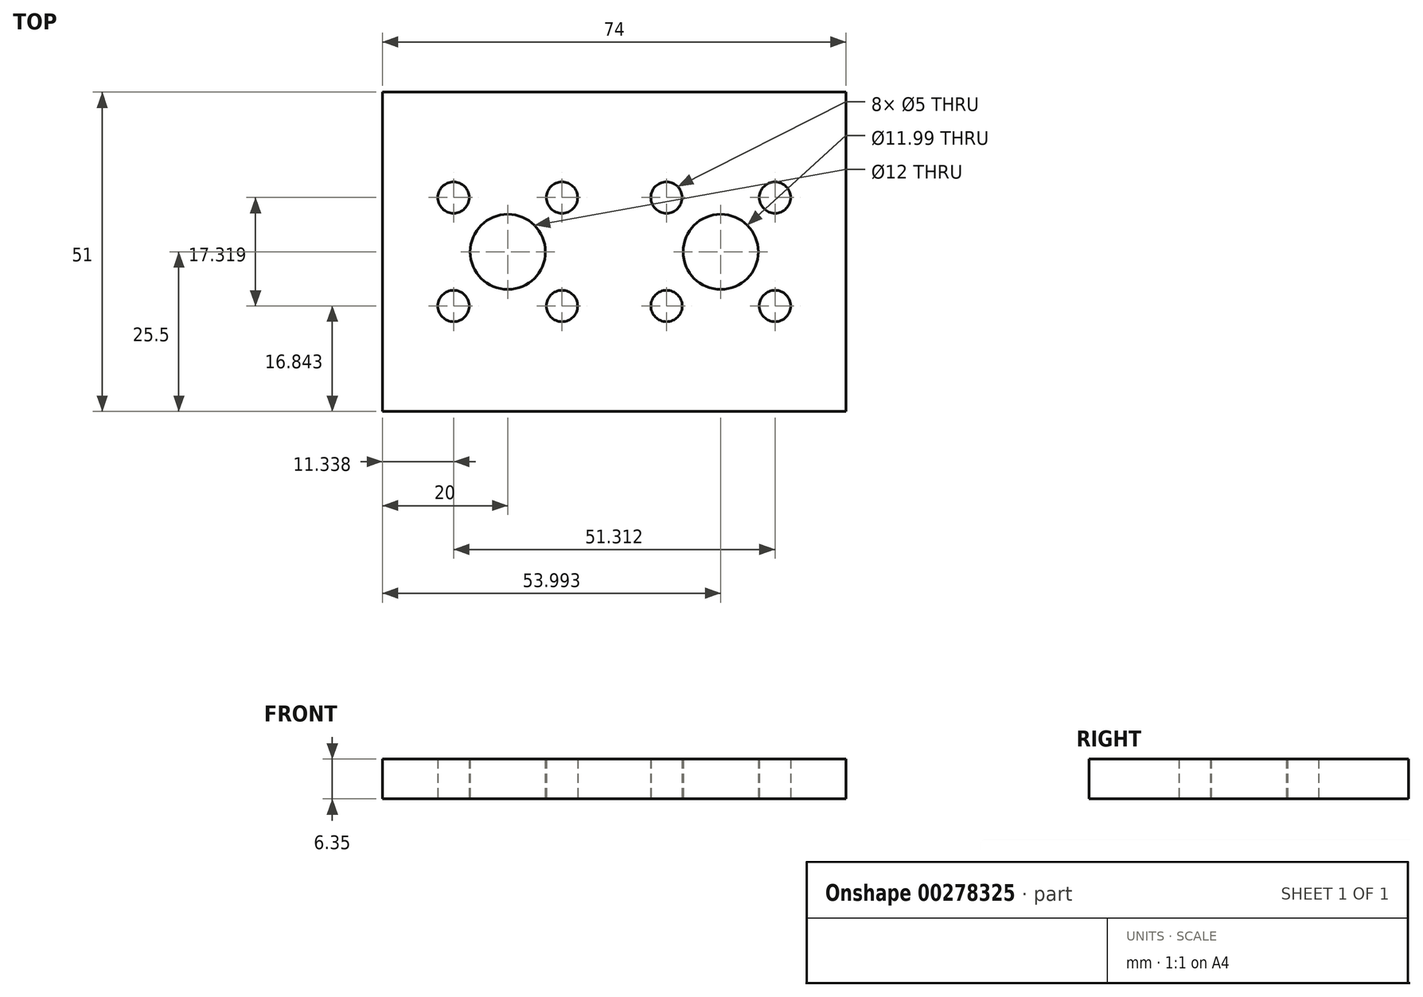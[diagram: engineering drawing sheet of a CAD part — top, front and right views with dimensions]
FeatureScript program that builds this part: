
annotation { "Feature Type Name" : "Feature", "Feature Type Description" : "" }
export const myFeature = defineFeature(function(context is Context, id is Id, definition is map)
    precondition{}
    {
        {
            var Q0;
            Q0=qCreatedBy(makeId("Top.planeOp"),FACE);
            var sketch = newSketch(context, id + "F0", { "sketchPlane" : qUnion([Q0])});
            skLineSegment(sketch, "E0.bottom", {"start": v(-37, -25.5) * mm, "end": v(37, -25.5) * mm});
            skLineSegment(sketch, "E0.top", {"start": v(-37, 25.5) * mm, "end": v(37, 25.5) * mm});
            skLineSegment(sketch, "E0.left", {"start": v(-37, -25.5) * mm, "end": v(-37, 25.5) * mm});
            skLineSegment(sketch, "E0.right", {"start": v(37, -25.5) * mm, "end": v(37, 25.5) * mm});
            skPoint(sketch, "E0.middle", {"position": v(0, 0) * mm});
            skLineSegment(sketch, "E1", {"start": v(-37, 0) * mm, "end": v(-17, 0) * mm});
            skPoint(sketch, "E1.endSnap0", {"position": v(-37, 0) * mm});
            skCircle(sketch, "E2", {"center": v(-17, 0) * mm, "radius": 6 * mm});
            skLineSegment(sketch, "E3", {"start": v(-17, 0) * mm, "end": v(0, 0) * mm});
            skLineSegment(sketch, "E4", {"start": v(0, 0) * mm, "end": v(17, 0) * mm});
            skCircle(sketch, "E5", {"center": v(17, 0) * mm, "radius": 6 * mm});
            skLineSegment(sketch, "E6", {"start": v(-17, 0) * mm, "end": v(-25.66, 8.66) * mm});
            skCircle(sketch, "E7", {"center": v(-25.66, 8.66) * mm, "radius": 2.5 * mm});
            skLineSegment(sketch, "E8", {"start": v(-17, 0) * mm, "end": v(-8.34, 8.66) * mm});
            skLineSegment(sketch, "E9", {"start": v(-17, 0) * mm, "end": v(-8.34, -8.66) * mm});
            skLineSegment(sketch, "E10", {"start": v(-17, 0) * mm, "end": v(-25.66, -8.66) * mm});
            skLineSegment(sketch, "E11", {"start": v(17, 0) * mm, "end": v(25.65, 8.66) * mm});
            skLineSegment(sketch, "E12", {"start": v(17, 0) * mm, "end": v(25.65, -8.66) * mm});
            skLineSegment(sketch, "E13", {"start": v(17, 0) * mm, "end": v(8.33, 8.66) * mm});
            skLineSegment(sketch, "E14", {"start": v(17, 0) * mm, "end": v(8.34, -8.66) * mm});
            skPoint(sketch, "E14.endSnap0", {"position": v(8.5, 0) * mm});
            skCircle(sketch, "E15", {"center": v(-8.34, 8.66) * mm, "radius": 2.5 * mm});
            skCircle(sketch, "E16", {"center": v(-8.34, -8.66) * mm, "radius": 2.5 * mm});
            skCircle(sketch, "E17", {"center": v(-25.66, -8.66) * mm, "radius": 2.5 * mm});
            skCircle(sketch, "E18", {"center": v(25.65, -8.66) * mm, "radius": 2.5 * mm});
            skCircle(sketch, "E19", {"center": v(25.65, 8.66) * mm, "radius": 2.5 * mm});
            skCircle(sketch, "E20", {"center": v(8.34, -8.66) * mm, "radius": 2.5 * mm});
            skCircle(sketch, "E21", {"center": v(8.33, 8.66) * mm, "radius": 2.5 * mm});
            skSolve(sketch);
        }
        {
            var Q0;
            {var subQ0=sQuery(id+"F0.wireOp",EDGE,"E0.bottom");Q0=makeQuery(id+"F0.imprint","IMPRINT",FACE,{"disambiguationData":[TD([[makeQuery(id+"F0.imprint","IMPRINT",EDGE,{"derivedFrom":subQ0}),1.0]])]});}
            extrude(context, id + "F1", {"entities" : qUnion([Q0]), "depth" : 6.35 * mm});
        }
    });
